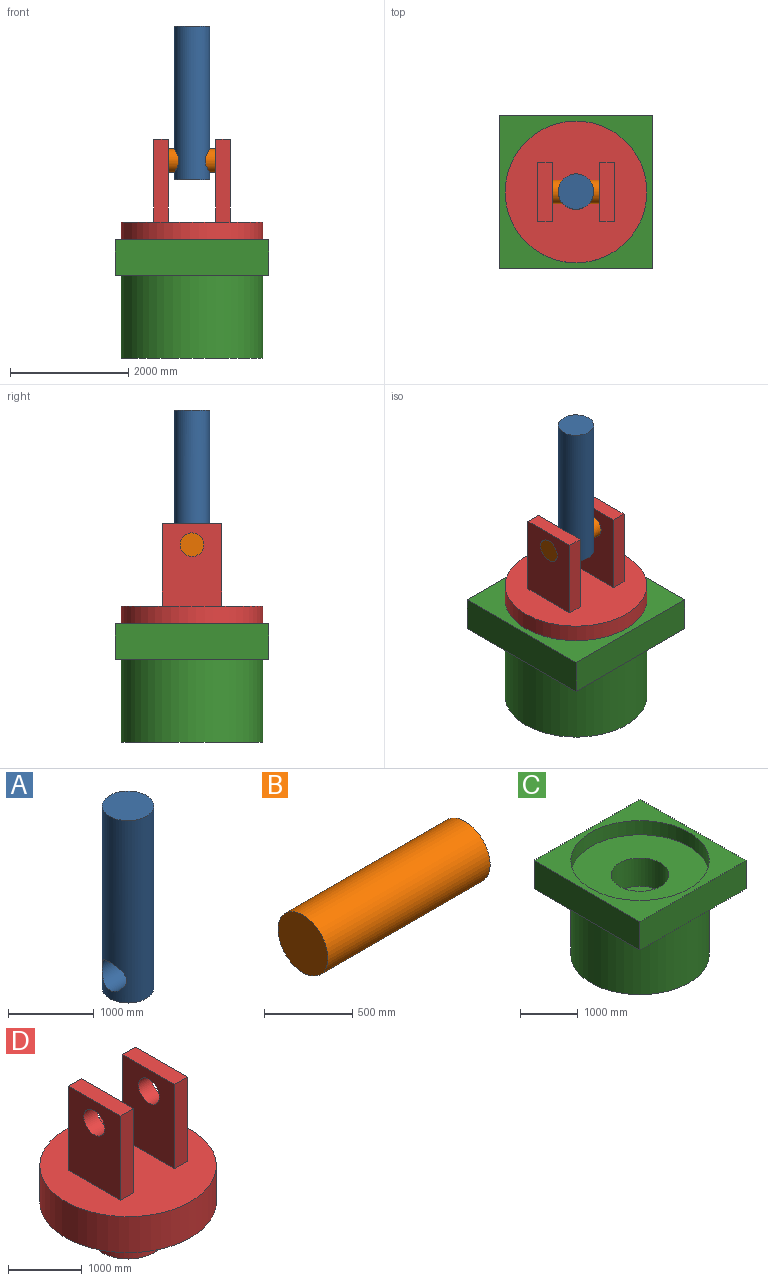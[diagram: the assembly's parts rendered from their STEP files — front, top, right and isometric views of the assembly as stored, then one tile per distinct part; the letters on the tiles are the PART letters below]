
ASSEMBLY  parts=4 mates=3
PART A: 4 faces, bbox 600x600x2600 mm
  f0: cylinder r=300mm len=2600mm, axis (0,0,-1), area 4632529.5mm2, adj f1,f2,f3
  f1: plane 600x600mm, normal (0,0,1), area 282743.3mm2, adj f0
  f2: plane 600x600mm, normal (0,0,-1), area 282743.3mm2, adj f0
  f3: cylinder r=200mm len=600mm, axis (1,0,0), area 661478mm2, adj f0
PART B: 3 faces, bbox 1300x400x400 mm
  f0: plane 400x400mm, normal (-1,0,0), area 125663.7mm2, adj f1
  f1: cylinder r=200mm len=1300mm, axis (1,0,0), area 1633628.2mm2, adj f0,f2
  f2: plane 400x400mm, normal (1,0,0), area 125663.7mm2, adj f1
PART C: 12 faces, bbox 2600x2600x2000 mm
  f0: plane 2600x600mm, normal (1,0,0), area 1560000mm2, adj f1,f3,f4,f5
  f1: plane 2600x600mm, normal (0,1,0), area 1560000mm2, adj f0,f2,f4,f5
  f2: plane 2600x600mm, normal (-1,0,0), area 1560000mm2, adj f1,f3,f4,f5
  f3: plane 2600x600mm, normal (0,-1,0), area 1560000mm2, adj f0,f2,f4,f5
  f4: plane 2600x2600mm, normal (0,0,1), area 2236106.6mm2, adj f0,f1,f2,f3,f8
  f5: plane 2600x2600mm, normal (0,0,-1), area 2236106.6mm2, adj f0,f1,f2,f3,f6
  f6: cylinder r=1200mm len=2400mm, axis (0,0,1), area 10555751.3mm2, adj f5,f7
  f7: plane 2400x2400mm, normal (0,0,-1), area 4523893.4mm2, adj f6
  f8: cylinder r=1200mm len=2400mm, axis (0,0,-1), area 2261946.7mm2, adj f4,f9
  f9: plane 2400x2400mm, normal (0,0,1), area 3738495.3mm2, adj f8,f10
  f10: cylinder r=500mm len=1000mm, axis (0,0,1), area 1884955.6mm2, adj f9,f11
  f11: plane 1000x1000mm, normal (0,0,1), area 785398.2mm2, adj f10
PART D: 17 faces, bbox 2400x2400x2600 mm
  f0: plane 2400x2400mm, normal (0,0,1), area 4023893.4mm2, adj f1,f3,f4,f5,f6,f8,f9,f10
  f1: cylinder r=1200mm len=2400mm, axis (0,0,-1), area 4523893.4mm2, adj f0,f2
  f2: plane 2400x2400mm, normal (0,0,-1), area 3738495.3mm2, adj f1,f13
  f3: plane 1400x1000mm, normal (-1,0,0), area 1274336.3mm2, adj f0,f4,f6,f7,f16
  f4: plane 1400x250mm, normal (0,-1,0), area 350000mm2, adj f0,f3,f5,f7
  f5: plane 1400x1000mm, normal (1,0,0), area 1274336.3mm2, adj f0,f4,f6,f7,f16
  f6: plane 1400x250mm, normal (0,1,0), area 350000mm2, adj f0,f3,f5,f7
  f7: plane 1000x250mm, normal (0,0,1), area 250000mm2, adj f3,f4,f5,f6
  f8: plane 1400x250mm, normal (0,1,0), area 350000mm2, adj f0,f9,f11,f12
  f9: plane 1400x1000mm, normal (-1,0,0), area 1274336.3mm2, adj f0,f8,f10,f12,f15
  f10: plane 1400x250mm, normal (0,-1,0), area 350000mm2, adj f0,f9,f11,f12
  f11: plane 1400x1000mm, normal (1,0,0), area 1274336.3mm2, adj f0,f8,f10,f12,f15
  f12: plane 1000x250mm, normal (0,0,1), area 250000mm2, adj f8,f9,f10,f11
  f13: cylinder r=500mm len=1000mm, axis (0,0,1), area 1884955.6mm2, adj f2,f14
  f14: plane 1000x1000mm, normal (0,0,-1), area 785398.2mm2, adj f13
  f15: cylinder r=200mm len=400mm, axis (1,0,0), area 314159.3mm2, adj f9,f11
  f16: cylinder r=200mm len=400mm, axis (1,0,0), area 314159.3mm2, adj f3,f5
PLACE A t=(-0.02,0,0)mm
PLACE B at identity
PLACE C at identity fixed
PLACE D rot(axis=(1,0,0),0deg) t=(0,0,0)mm
MATE fastened A.f3 <-> B.f1  axis (1,0,0) through (0,0,1940)mm
MATE revolute D.f1 <-> C.f6  axis (0,0,-1) through (0,0,-300)mm
MATE revolute B.f1 <-> D.f15  axis (1,0,0) through (650,0,1940)mm
